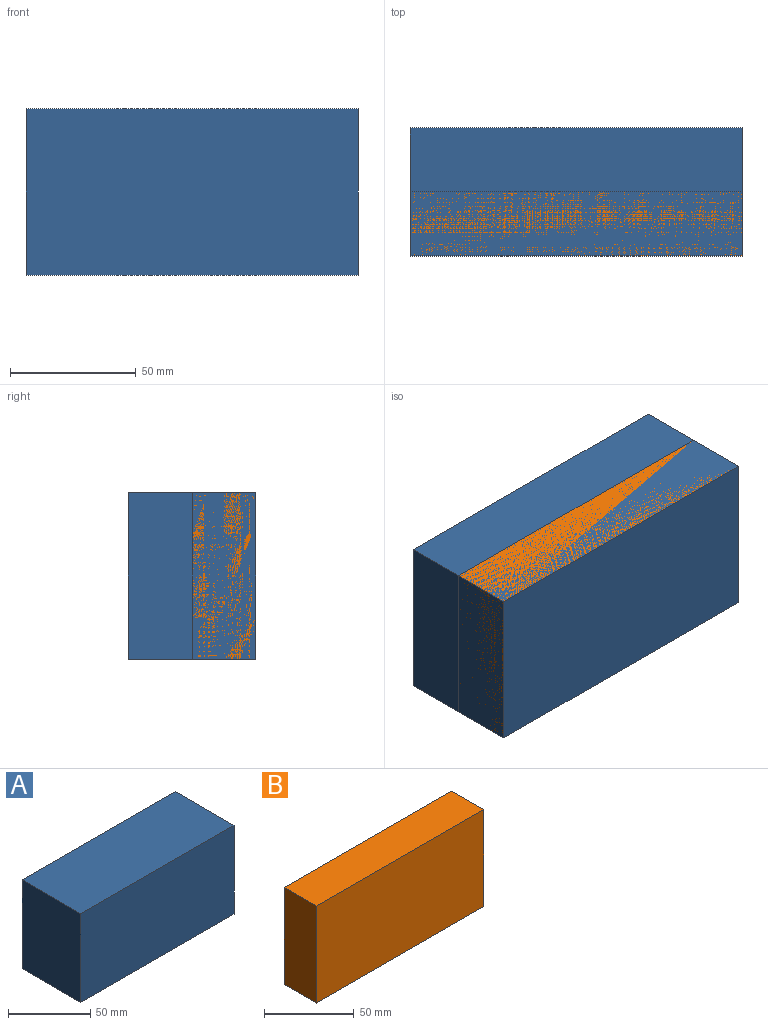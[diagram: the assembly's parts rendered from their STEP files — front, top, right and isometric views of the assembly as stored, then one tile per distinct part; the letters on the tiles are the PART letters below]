
ASSEMBLY  parts=2 mates=1
PART A: 6 faces, bbox 132x50.8x66.3 mm
  f0: plane 131.98x50.8mm, normal (0,0,1), area 6704.5mm2, adj f1,f3,f4,f5
  f1: plane 66.26x50.8mm, normal (-1,0,0), area 3365.9mm2, adj f0,f2,f4,f5
  f2: plane 131.98x50.8mm, normal (0,0,-1), area 6704.5mm2, adj f1,f3,f4,f5
  f3: plane 66.26x50.8mm, normal (1,0,0), area 3365.9mm2, adj f0,f2,f4,f5
  f4: plane 131.98x66.26mm, normal (0,-1,0), area 8744.6mm2, adj f0,f1,f2,f3
  f5: plane 131.98x66.26mm, normal (0,1,0), area 8744.6mm2, adj f0,f1,f2,f3
PART B: 6 faces, bbox 132x25.4x66.3 mm
  f0: plane 131.98x25.4mm, normal (0,0,1), area 3352.2mm2, adj f1,f3,f4,f5
  f1: plane 66.26x25.4mm, normal (-1,0,0), area 1683mm2, adj f0,f2,f4,f5
  f2: plane 131.98x25.4mm, normal (0,0,-1), area 3352.2mm2, adj f1,f3,f4,f5
  f3: plane 66.26x25.4mm, normal (1,0,0), area 1683mm2, adj f0,f2,f4,f5
  f4: plane 131.98x66.26mm, normal (0,-1,0), area 8744.6mm2, adj f0,f1,f2,f3
  f5: plane 131.98x66.26mm, normal (0,1,0), area 8744.6mm2, adj f0,f1,f2,f3
PLACE A at identity
PLACE B t=(0,-25.4,0)mm
MATE slider B.f4 <-> A.f4  axis (0,-1,0) through (-74.56,-50.8,8.32)mm
